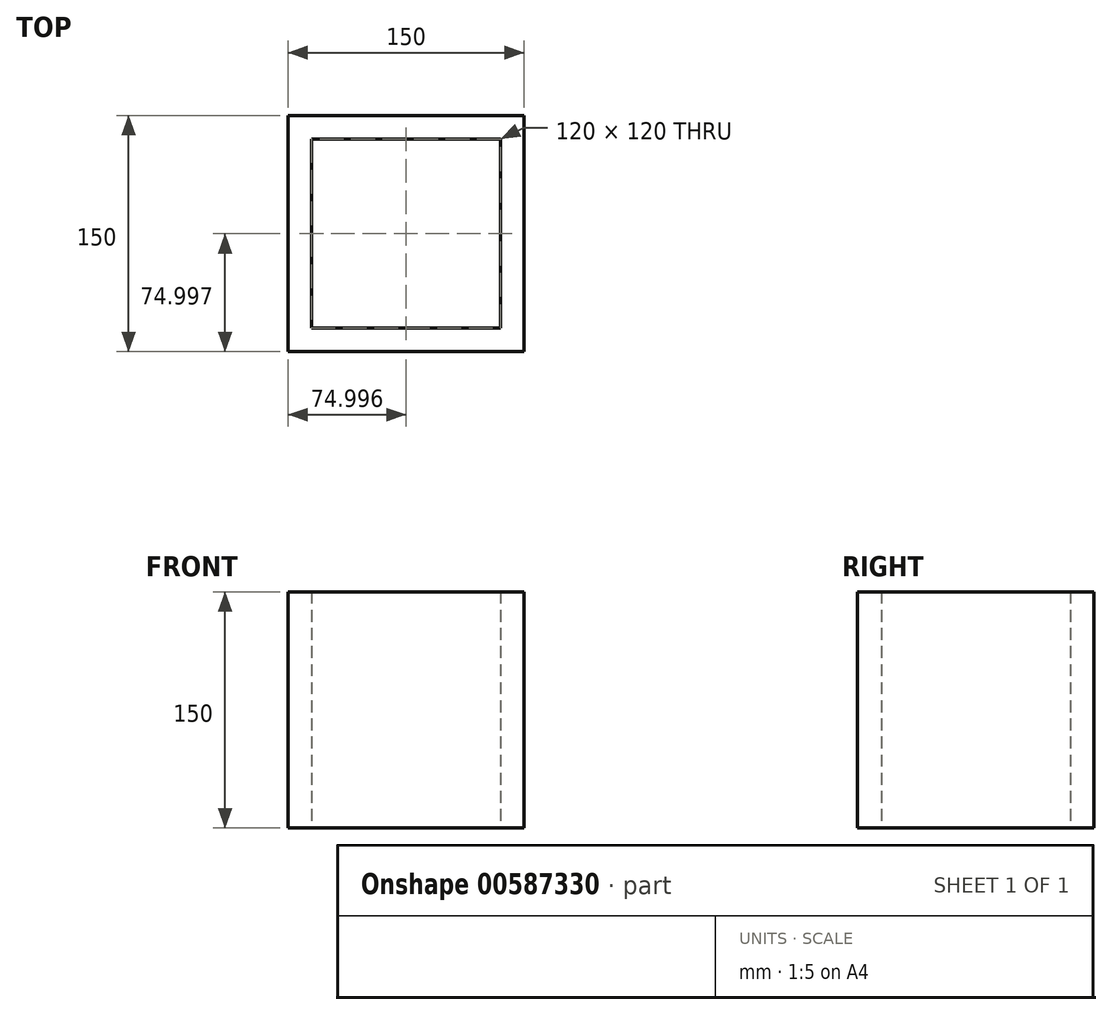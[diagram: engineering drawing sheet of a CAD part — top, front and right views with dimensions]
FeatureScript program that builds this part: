
annotation { "Feature Type Name" : "Feature", "Feature Type Description" : "" }
export const myFeature = defineFeature(function(context is Context, id is Id, definition is map)
    precondition{}
    {
        {
            var Q0;
            Q0=qCreatedBy(makeId("Top.planeOp"),FACE);
            var sketch = newSketch(context, id + "F0", { "sketchPlane" : qUnion([Q0])});
            skLineSegment(sketch, "E0.bottom", {"start": v(-58.65, 45.53) * mm, "end": v(-208.65, 45.53) * mm});
            skLineSegment(sketch, "E0.top", {"start": v(-58.65, -104.47) * mm, "end": v(-208.65, -104.47) * mm});
            skLineSegment(sketch, "E0.left", {"start": v(-58.65, 45.53) * mm, "end": v(-58.65, -104.47) * mm});
            skLineSegment(sketch, "E0.right", {"start": v(-208.65, 45.53) * mm, "end": v(-208.65, -104.47) * mm});
            skSolve(sketch);
        }
        {
            var Q0;
            Q0=makeQuery(id+"F0.imprint","IMPRINT",FACE,{"disambiguationData":[TD([[makeQuery(id+"F0.imprint","IMPRINT",EDGE,{"derivedFrom":sQuery(id+"F0.wireOp",EDGE,"E0.bottom")}),1.0]])]});
            extrude(context, id + "F1", {"entities" : qUnion([Q0]), "depth" : 150 * mm, "offsetDistance" : 25 * mm});
        }
        {
            var Q0;
            Q0=makeQuery(id+"F1.opExtrude","CAP_FACE",FACE,{"disambiguationData":[OSD([sQuery(id+"F0.wireOp",EDGE,"E0.bottom"),sQuery(id+"F0.wireOp",EDGE,"E0.top"),sQuery(id+"F0.wireOp",EDGE,"E0.left"),sQuery(id+"F0.wireOp",EDGE,"E0.right")])],"isStart":true});
            var Q1;
            Q1=makeQuery(id+"F1.opExtrude","CAP_FACE",FACE,{"disambiguationData":[OSD([sQuery(id+"F0.wireOp",EDGE,"E0.bottom"),sQuery(id+"F0.wireOp",EDGE,"E0.top"),sQuery(id+"F0.wireOp",EDGE,"E0.left"),sQuery(id+"F0.wireOp",EDGE,"E0.right")])],"isStart":false});
            shell(context, id + "F2", {"entities" : qUnion([Q0, Q1]), "thickness" : 15 * mm});
        }
    });
